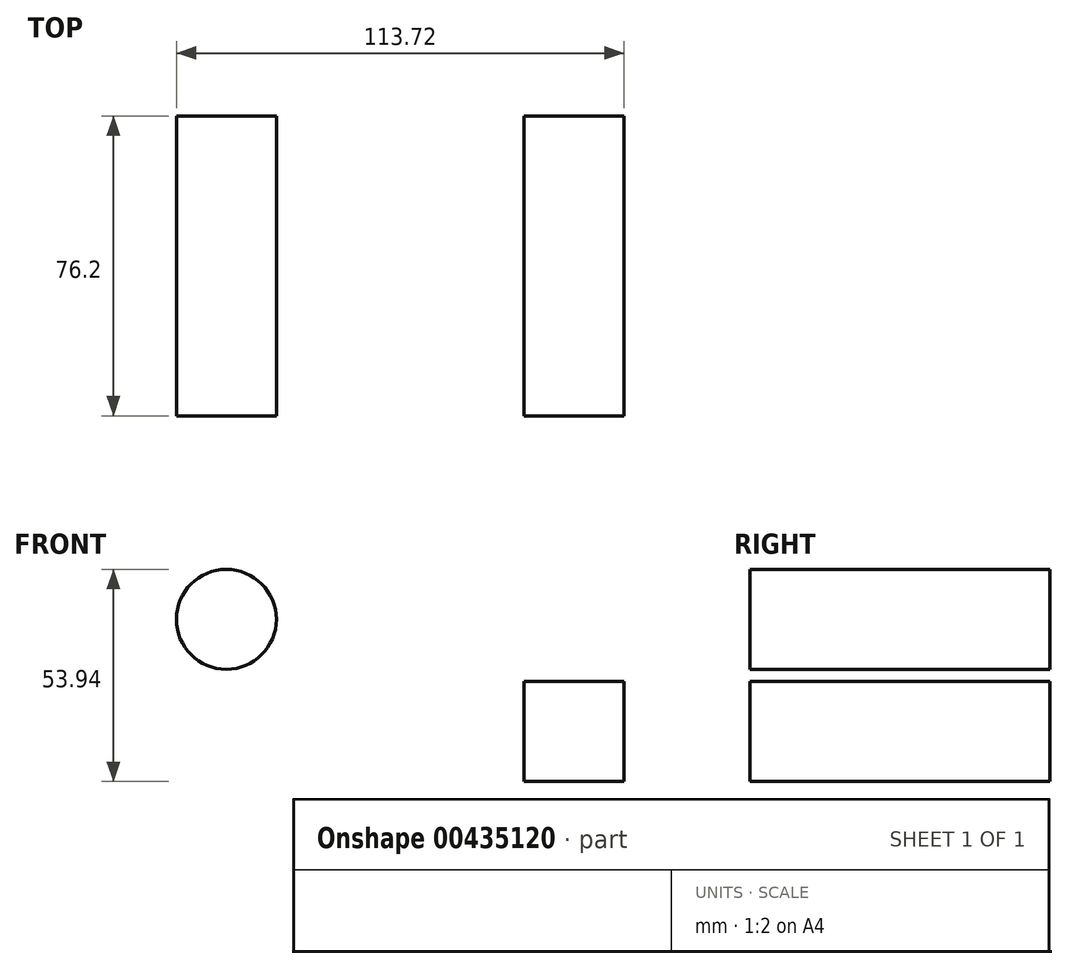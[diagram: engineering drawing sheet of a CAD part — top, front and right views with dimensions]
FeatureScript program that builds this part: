
annotation { "Feature Type Name" : "Feature", "Feature Type Description" : "" }
export const myFeature = defineFeature(function(context is Context, id is Id, definition is map)
    precondition{}
    {
        {
            var Q0;
            Q0=qCreatedBy(makeId("Front.planeOp"),FACE);
            var sketch = newSketch(context, id + "F0", { "sketchPlane" : qUnion([Q0])});
            skLineSegment(sketch, "E0.bottom", {"start": v(7.54, 29.03) * mm, "end": v(32.94, 29.03) * mm});
            skLineSegment(sketch, "E0.top", {"start": v(7.54, 3.63) * mm, "end": v(32.94, 3.63) * mm});
            skLineSegment(sketch, "E0.left", {"start": v(7.54, 29.03) * mm, "end": v(7.54, 3.63) * mm});
            skLineSegment(sketch, "E0.right", {"start": v(32.94, 29.03) * mm, "end": v(32.94, 3.63) * mm});
            skCircle(sketch, "E1", {"center": v(-68.08, 44.87) * mm, "radius": 12.7 * mm});
            skSolve(sketch);
        }
        {
            var Q0;
            Q0 = qSketchRegion(id + "F0", true);
            extrude(context, id + "F1", {"entities" : qUnion([Q0]), "depth" : 76.2 * mm});
        }
    });
